MODEL slx_1dac27b51b91
CONFIG AbsTol = auto
CONFIG EnableMultiTasking = on
CONFIG FixedStep = 0.001
CONFIG MaxStep = auto
CONFIG MinStep = auto
CONFIG RelTol = 1e-3
CONFIG SampleTimeConstraint = Unconstrained
CONFIG Solver = ode14x
CONFIG SolverName = ode14x
CONFIG StartTime = 0.0
CONFIG StopTime = 15
BLOCK [SubSystem] Cascade
  Ports = []
  RequestExecContextInheritance = off
BLOCK [From] Cascade/Actual ouput
  GotoTag = Y
BLOCK [Sum] Cascade/Add1
  IconShape = rectangular
  Ports = [2, 1]
BLOCK [From] Cascade/Disturbance Input
  GotoTag = D
BLOCK [From] Cascade/Error
  GotoTag = E
BLOCK [Gain] Cascade/Force to Voltage
  Gain = 1/ 2871.14
BLOCK [FromWorkspace] Cascade/From Workspace2
  OutDataTypeStr = double
  OutputAfterFinalValue = Setting to zero
  VariableName = Cut1500down
BLOCK [Gain] Cascade/Gain3
  Gain = gain_P
BLOCK [Gain] Cascade/Gain4
  Gain = gain_V_I
BLOCK [Gain] Cascade/Gain5
  Gain = gain_V_P
BLOCK [Goto] Cascade/Goto
  GotoTag = D
BLOCK [Goto] Cascade/Goto1
  GotoTag = R
BLOCK [Goto] Cascade/Goto2
  GotoTag = E
BLOCK [Goto] Cascade/Goto3
  GotoTag = Y
BLOCK [Integrator] Cascade/Integrator1
  InitialCondition = .1
  Ports = [1, 1]
BLOCK [ManualSwitch] Cascade/Manual Switch
  NameLocation = left
BLOCK [Scope] Cascade/Output Position (mm)
  Floating = off
  NumInputPorts = 1
  Ports = [1]
  ScopeSpecificationString = Simulink.scopes.TimeScopeBlockCfg('CurrentConfiguration', extmgr.ConfigurationSet(extmgr.Configuration('Core','General UI',true),extmgr.Configuration('Core','Source UI',true),extmgr.Configuration('Sources','WiredSimulink',true,'DataLoggingVariableName','ScopeData2'),extmgr.Configuration('Visuals','Time Domain',true,'SerializedDisplays',{struct('MinYLimReal','-66692021064882830098913468871871206665...<+3796ch>
BLOCK [TransferFcn] Cascade/Plant (Googol Tech)
  Denominator = [1 163 193.3]
  Numerator = [78020]
BLOCK [Sin] Cascade/Ref. Position, Xref (mm)
  Amplitude = 5
  Frequency = 0.5*(2*pi)
  Offset = 1/2000
  Ports = [0, 1]
  SampleTime = 0
BLOCK [From] Cascade/Reference Input
  GotoTag = R
BLOCK [Saturate] Cascade/Saturation
  LowerLimit = -92
  UpperLimit = 92
BLOCK [Scope] Cascade/Scope
  Floating = off
  NumInputPorts = 4
  Ports = [4]
  ScopeSpecificationString = Simulink.scopes.TimeScopeBlockCfg('CurrentConfiguration', extmgr.ConfigurationSet(extmgr.Configuration('Core','General UI',true),extmgr.Configuration('Core','Source UI',true),extmgr.Configuration('Sources','WiredSimulink',true,'DataLoggingVariableName','cascade','DataLogging',true,'DataLoggingSaveFormat','StructureWithTime'),extmgr.Configuration('Visuals','Time Domain',true,'SerializedDisplays',{s...<+3904ch>
BLOCK [Sum] Cascade/Sum1
  Inputs = ++|
  Ports = [2, 1]
BLOCK [Sum] Cascade/Sum3
  Inputs = |+-
  NameLocation = top
  Ports = [2, 1]
BLOCK [Sum] Cascade/Sum4
  Inputs = |+-
  NameLocation = top
  Ports = [2, 1]
BLOCK [TransportDelay] Cascade/TIme Delay
  DelayTime = 0.0012
  Ports = [1, 1]
BLOCK [TransferFcn] Cascade/V est
  Denominator = [1 942.5]
  Numerator = [942.5, 0]
BLOCK [SubSystem] Model Based Design
  Commented = on
  Ports = [0, 0, 0, 0, 0, 1]
  RequestExecContextInheritance = off
BLOCK [Scope] Model Based Design/Axis Cmd
  Floating = off
  NumInputPorts = 2
  Ports = [2]
  ScopeSpecificationString = Simulink.scopes.TimeScopeBlockCfg('CurrentConfiguration', extmgr.ConfigurationSet(extmgr.Configuration('Core','General UI',true),extmgr.Configuration('Core','Source UI',true),extmgr.Configuration('Sources','WiredSimulink',true),extmgr.Configuration('Visuals','Time Domain',true,'SerializedDisplays',{struct('MinYLimReal','-0.06054','MaxYLimReal','0.06145','YLabelReal','','MinYLimMag','0.00000','MaxY...<+1365ch>
BLOCK [Reference] Model Based Design/Base  REF=sm_lib/Body Elements/Brick Solid
  Ports = [0, 0, 0, 0, 0, 1, 1]
  SourceBlock = sm_lib/Body Elements/Brick Solid
  SourceProductBaseCode = MS
  SourceType = Brick Solid
BLOCK [From] Model Based Design/From
  GotoTag = Ycmd
  TagVisibility = global
BLOCK [From] Model Based Design/From1
  GotoTag = Xcmd
  TagVisibility = global
BLOCK [From] Model Based Design/From2
  GotoTag = Ycmd
  TagVisibility = global
BLOCK [From] Model Based Design/From3
  GotoTag = Xcmd
  TagVisibility = global
BLOCK [From] Model Based Design/From4
  GotoTag = Px
  TagVisibility = global
BLOCK [From] Model Based Design/From5
  GotoTag = Vx
  TagVisibility = global
BLOCK [From] Model Based Design/From6
  GotoTag = Py
  TagVisibility = global
BLOCK [From] Model Based Design/From7
  GotoTag = Vy
  TagVisibility = global
BLOCK [From] Model Based Design/From8
  GotoTag = Px
  TagVisibility = global
BLOCK [From] Model Based Design/From9
  GotoTag = Py
  TagVisibility = global
BLOCK [Goto] Model Based Design/Goto
  GotoTag = Px
  TagVisibility = global
BLOCK [Goto] Model Based Design/Goto1
  GotoTag = Vx
  TagVisibility = global
BLOCK [Goto] Model Based Design/Goto2
  GotoTag = Py
  TagVisibility = global
BLOCK [Goto] Model Based Design/Goto3
  GotoTag = Vy
  TagVisibility = global
BLOCK [Reference] Model Based Design/PS-Simulink Converter  REF=nesl_utility/PS-Simulink
Converter
  Ports = [0, 1, 0, 0, 0, 1]
  SourceBlock = nesl_utility/PS-Simulink
Converter
  SourceProductBaseCode = SS
  SourceType = PS-Simulink
Converter
BLOCK [Reference] Model Based Design/PS-Simulink Converter1  REF=nesl_utility/PS-Simulink
Converter
  Ports = [0, 1, 0, 0, 0, 1]
  SourceBlock = nesl_utility/PS-Simulink
Converter
  SourceProductBaseCode = SS
  SourceType = PS-Simulink
Converter
BLOCK [Reference] Model Based Design/PS-Simulink Converter2  REF=nesl_utility/PS-Simulink
Converter
  Ports = [0, 1, 0, 0, 0, 1]
  SourceBlock = nesl_utility/PS-Simulink
Converter
  SourceProductBaseCode = SS
  SourceType = PS-Simulink
Converter
BLOCK [Reference] Model Based Design/PS-Simulink Converter3  REF=nesl_utility/PS-Simulink
Converter
  Ports = [0, 1, 0, 0, 0, 1]
  SourceBlock = nesl_utility/PS-Simulink
Converter
  SourceProductBaseCode = SS
  SourceType = PS-Simulink
Converter
BLOCK [Scope] Model Based Design/Position, Velocity
  Floating = off
  NumInputPorts = 4
  Ports = [4]
  ScopeSpecificationString = Simulink.scopes.TimeScopeBlockCfg('CurrentConfiguration', extmgr.ConfigurationSet(extmgr.Configuration('Core','General UI',true),extmgr.Configuration('Core','Source UI',true),extmgr.Configuration('Sources','WiredSimulink',true,'DataLoggingVariableName','ScopeData1'),extmgr.Configuration('Visuals','Time Domain',true,'SerializedDisplays',{struct('MinYLimReal','-0.0575','MaxYLimReal','0.0575','YLabel...<+3923ch>
BLOCK [Reference] Model Based Design/Prismatic X-axis  REF=sm_lib/Joints/Prismatic
Joint
  Ports = [0, 0, 0, 0, 0, 2, 3]
  SourceBlock = sm_lib/Joints/Prismatic
Joint
  SourceProductBaseCode = MS
  SourceType = Prismatic
Joint
BLOCK [Reference] Model Based Design/Prismatic Y-axis  REF=sm_lib/Joints/Prismatic
Joint
  Ports = [0, 0, 0, 0, 0, 2, 3]
  SourceBlock = sm_lib/Joints/Prismatic
Joint
  SourceProductBaseCode = MS
  SourceType = Prismatic
Joint
BLOCK [Reference] Model Based Design/Rigid Transform1  REF=sm_lib/Frames and
Transforms/Rigid
Transform
  Ports = [0, 0, 0, 0, 0, 1, 1]
  SourceBlock = sm_lib/Frames and
Transforms/Rigid
Transform
  SourceProductBaseCode = MS
  SourceType = Rigid
Transform
BLOCK [SubSystem] Model Based Design/S2m
  Ports = [1, 0, 0, 0, 0, 0, 1]
  RequestExecContextInheritance = off
  ShowPortLabels = none
BLOCK [Inport] Model Based Design/S2m/In
BLOCK [PMIOPort] Model Based Design/S2m/Out
  Side = Right
BLOCK [Reference] Model Based Design/S2m/mm  REF=nesl_utility/Simulink-PS
Converter
  Ports = [1, 0, 0, 0, 0, 0, 1]
  SourceBlock = nesl_utility/Simulink-PS
Converter
  SourceProductBaseCode = MT,SS
  SourceType = Simulink-PS
Converter
BLOCK [SubSystem] Model Based Design/S2m1
  Ports = [1, 0, 0, 0, 0, 0, 1]
  RequestExecContextInheritance = off
  ShowPortLabels = none
BLOCK [Inport] Model Based Design/S2m1/In
BLOCK [PMIOPort] Model Based Design/S2m1/Prismatic Y-axis
  Side = Right
BLOCK [Reference] Model Based Design/S2m1/mm  REF=nesl_utility/Simulink-PS
Converter
  Ports = [1, 0, 0, 0, 0, 0, 1]
  SourceBlock = nesl_utility/Simulink-PS
Converter
  SourceProductBaseCode = MT,SS
  SourceType = Simulink-PS
Converter
BLOCK [SubSystem] Model Based Design/Subsystem
  Ports = []
  RequestExecContextInheritance = off
BLOCK [Reference] Model Based Design/Subsystem/Band-Limited White Noise  REF=simulink/Sources/Band-Limited
White Noise
  NameLocation = right
  Ports = [0, 1]
  SourceBlock = simulink/Sources/Band-Limited
White Noise
  SourceProductBaseCode = SL
  SourceType = Band-Limited White Noise.
BLOCK [Goto] Model Based Design/Subsystem/Goto
  GotoTag = Ycmd
  TagVisibility = global
BLOCK [Goto] Model Based Design/Subsystem/Goto1
  GotoTag = Xcmd
  TagVisibility = global
BLOCK [Saturate] Model Based Design/Subsystem/Saturation
  LowerLimit = -.2
  UpperLimit = .2
BLOCK [Saturate] Model Based Design/Subsystem/Saturation1
  LowerLimit = -.1
  UpperLimit = .1
BLOCK [Sin] Model Based Design/Subsystem/Sine Wave X
  Amplitude = ax
  Frequency = Fx
  Ports = [0, 1]
  SampleTime = 0
BLOCK [Sin] Model Based Design/Subsystem/Sine Wave Y
  Amplitude = ay
  Frequency = Fy
  Phase = 8
  Ports = [0, 1]
  SampleTime = 0
BLOCK [Sum] Model Based Design/Subsystem/Sum
  Inputs = |++
  Ports = [2, 1]
BLOCK [TransferFcn] Model Based Design/Subsystem/Transfer Fcn
  Denominator = [1 163 193.3]
  Numerator = [72080]
BLOCK [TransportDelay] Model Based Design/Subsystem/Transport Delay2
  DelayTime = 0.0012
  Ports = [1, 1]
BLOCK [SubSystem] Model Based Design/World Config
  NameLocation = top
  Ports = [0, 0, 0, 0, 0, 0, 1]
  RequestExecContextInheritance = off
BLOCK [Reference] Model Based Design/World Config/Mechanism Configuration  REF=sm_lib/Utilities/Mechanism
Configuration
  Ports = [0, 0, 0, 0, 0, 0, 1]
  SourceBlock = sm_lib/Utilities/Mechanism
Configuration
  SourceProductBaseCode = MS
  SourceType = Mechanism
Configuration
BLOCK [PMIOPort] Model Based Design/World Config/Mechanism Configuration1
  Side = Right
BLOCK [Reference] Model Based Design/World Config/Solver Configuration  REF=nesl_utility/Solver
Configuration
  Ports = [0, 0, 0, 0, 0, 0, 1]
  SourceBlock = nesl_utility/Solver
Configuration
  SourceProductBaseCode = MT,SS
  SourceType = Solver
Configuration
BLOCK [Reference] Model Based Design/World Config/World Frame  REF=sm_lib/Frames and
Transforms/World Frame
  Ports = [0, 0, 0, 0, 0, 0, 1]
  SourceBlock = sm_lib/Frames and
Transforms/World Frame
  SourceProductBaseCode = MS
  SourceType = World Frame
BLOCK [Reference] Model Based Design/X-axis  REF=sm_lib/Body Elements/Brick Solid
  Ports = [0, 0, 0, 0, 0, 1, 1]
  SourceBlock = sm_lib/Body Elements/Brick Solid
  SourceProductBaseCode = MS
  SourceType = Brick Solid
BLOCK [Reference] Model Based Design/XY Position  REF=simulink/Sinks/XY Graph
  Ports = [2]
  SourceBlock = simulink/Sinks/XY Graph
  SourceProductBaseCode = SL
  SourceType = XY scope.
BLOCK [Reference] Model Based Design/Y-axis  REF=sm_lib/Body Elements/Brick Solid
  Ports = [0, 0, 0, 0, 0, 1, 1]
  SourceBlock = sm_lib/Body Elements/Brick Solid
  SourceProductBaseCode = MS
  SourceType = Brick Solid
BLOCK [Reference] Model Based Design/Y-axis Transform  REF=sm_lib/Frames and
Transforms/Rigid
Transform
  Ports = [0, 0, 0, 0, 0, 1, 1]
  SourceBlock = sm_lib/Frames and
Transforms/Rigid
Transform
  SourceProductBaseCode = MS
  SourceType = Rigid
Transform
BLOCK [Reference] Model Based Design/Y-top  REF=sm_lib/Body Elements/Brick Solid
  Ports = [0, 0, 0, 0, 0, 1, 1]
  SourceBlock = sm_lib/Body Elements/Brick Solid
  SourceProductBaseCode = MS
  SourceType = Brick Solid
BLOCK [PMIOPort] Model Based Design/Y-top1
  Side = Left
BLOCK [SubSystem] PID
  Commented = on
  Ports = []
  RequestExecContextInheritance = off
BLOCK [From] PID/Actual ouput
  GotoTag = Y
BLOCK [Scope] PID/Actual position
  Floating = off
  NumInputPorts = 1
  Ports = [1]
  ScopeSpecificationString = Simulink.scopes.TimeScopeBlockCfg('CurrentConfiguration', extmgr.ConfigurationSet(extmgr.Configuration('Core','General UI',true),extmgr.Configuration('Core','Source UI',true),extmgr.Configuration('Sources','WiredSimulink',true,'DataLoggingVariableName','PID_ActualPosition','DataLoggingSaveFormat','Array'),extmgr.Configuration('Visuals','Time Domain',true,'SerializedDisplays',{struct('MinYLimReal',...<+1431ch>
BLOCK [Sum] PID/Add
  IconShape = rectangular
  Inputs = +++
  Ports = [3, 1]
BLOCK [Derivative] PID/Derivative
BLOCK [From] PID/Disturbance Input
  GotoTag = D
BLOCK [From] PID/Error
  GotoTag = E
BLOCK [Gain] PID/Force to Voltage
  Gain = 1/ 2871.14
BLOCK [FromWorkspace] PID/From Workspace2
  OutDataTypeStr = double
  OutputAfterFinalValue = Setting to zero
  VariableName = Cut1500down
BLOCK [Gain] PID/Gain
  Gain = new_kd
BLOCK [Gain] PID/Gain1
  Gain = new_ki
BLOCK [Gain] PID/Gain2
  Gain = new_kp
  NameLocation = right
BLOCK [Goto] PID/Goto
  GotoTag = D
BLOCK [Goto] PID/Goto1
  GotoTag = R
BLOCK [Goto] PID/Goto2
  GotoTag = E
BLOCK [Goto] PID/Goto3
  GotoTag = Y
BLOCK [Integrator] PID/Integrator
  Ports = [1, 1]
BLOCK [ManualSwitch] PID/Manual Switch1
  CurrentSetting = 0
  NameLocation = left
BLOCK [TransferFcn] PID/Plant (Googol Tech)
  Denominator = [1 163 193.3]
  Numerator = [78020]
BLOCK [Sin] PID/Ref. Position, Xref (mm)
  Amplitude = 5
  Frequency = 0.5*(2*pi)
  Offset = 1/2000
  Ports = [0, 1]
  SampleTime = 0
BLOCK [From] PID/Reference Input
  GotoTag = R
BLOCK [Saturate] PID/Saturation1
  LowerLimit = -92
  UpperLimit = 92
BLOCK [Scope] PID/Scope
  Floating = off
  NumInputPorts = 4
  Ports = [4]
  ScopeSpecificationString = Simulink.scopes.TimeScopeBlockCfg('CurrentConfiguration', extmgr.ConfigurationSet(extmgr.Configuration('Core','General UI',true),extmgr.Configuration('Core','Source UI',true),extmgr.Configuration('Sources','WiredSimulink',true,'DataLoggingVariableName','PID','DataLogging',true,'DataLoggingSaveFormat','StructureWithTime'),extmgr.Configuration('Visuals','Time Domain',true,'SerializedDisplays',{struc...<+3842ch>
BLOCK [Sum] PID/Sum
  Inputs = ++|
  Ports = [2, 1]
BLOCK [Sum] PID/Sum2
  Inputs = |+-
  NameLocation = top
  Ports = [2, 1]
BLOCK [TransportDelay] PID/TIme Delay
  DelayTime = 0.0012
  Ports = [1, 1]
BLOCK [SubSystem] SMC
  Commented = on
  Ports = []
  RequestExecContextInheritance = off
BLOCK [From] SMC/Actual ouput
  GotoTag = Y
BLOCK [Scope] SMC/Actual position
  Floating = off
  NumInputPorts = 1
  Ports = [1]
  ScopeSpecificationString = Simulink.scopes.TimeScopeBlockCfg('CurrentConfiguration', extmgr.ConfigurationSet(extmgr.Configuration('Core','General UI',true),extmgr.Configuration('Core','Source UI',true),extmgr.Configuration('Sources','WiredSimulink',true,'DataLoggingVariableName','ScopeData1'),extmgr.Configuration('Visuals','Time Domain',true,'SerializedDisplays',{struct('MinYLimReal','-235.24396','MaxYLimReal','662.41077','...<+1446ch>
BLOCK [Scope] SMC/Actual position1
  Commented = on
  Floating = off
  NumInputPorts = 1
  Ports = [1]
  ScopeSpecificationString = Simulink.scopes.TimeScopeBlockCfg('CurrentConfiguration', extmgr.ConfigurationSet(extmgr.Configuration('Core','General UI',true),extmgr.Configuration('Core','Source UI',true),extmgr.Configuration('Sources','WiredSimulink',true,'DataLoggingVariableName','ScopeData1'),extmgr.Configuration('Visuals','Time Domain',true,'SerializedDisplays',{struct('MinYLimReal','-32969.8446','MaxYLimReal','32938.39501...<+1458ch>
BLOCK [Sum] SMC/Add
  IconShape = rectangular
  Inputs = -+
  Ports = [2, 1]
BLOCK [Sum] SMC/Add1
  IconShape = rectangular
  Inputs = +-
  NameLocation = top
  Ports = [2, 1]
BLOCK [Sum] SMC/Add10
  Commented = on
  IconShape = rectangular
  Inputs = +-
  Ports = [2, 1]
BLOCK [Sum] SMC/Add2
  IconShape = rectangular
  Ports = [2, 1]
BLOCK [Sum] SMC/Add3
  IconShape = rectangular
  Inputs = -+
  Ports = [2, 1]
BLOCK [Sum] SMC/Add4
  IconShape = rectangular
  Inputs = +++-
  NameLocation = top
  Ports = [4, 1]
BLOCK [Sum] SMC/Add5
  Commented = on
  IconShape = rectangular
  Inputs = +-
  Ports = [2, 1]
BLOCK [Sum] SMC/Add6
  Commented = on
  IconShape = rectangular
  Inputs = +-
  Ports = [2, 1]
BLOCK [Sum] SMC/Add8
  Commented = on
  IconShape = rectangular
  Inputs = -+
  Ports = [2, 1]
BLOCK [Sum] SMC/Add9
  Commented = on
  IconShape = rectangular
  Inputs = ++++++
  NameLocation = top
  Ports = [6, 1]
BLOCK [Derivative] SMC/Derivative1
  NameLocation = left
BLOCK [From] SMC/Disturbance Input
  GotoTag = D
BLOCK [From] SMC/Error
  GotoTag = E
BLOCK [Gain] SMC/Force to Voltage1
  Gain = 1/ 2871.14
BLOCK [Gain] SMC/Force to Voltage2
  Commented = on
  Gain = 1/ 2871.14
BLOCK [FromWorkspace] SMC/From Workspace1
  Commented = on
  OutDataTypeStr = double
  OutputAfterFinalValue = Setting to zero
  VariableName = Cut1500down
BLOCK [FromWorkspace] SMC/From Workspace2
  OutDataTypeStr = double
  OutputAfterFinalValue = Setting to zero
  VariableName = Cut1500down
BLOCK [Gain] SMC/Gain
  Gain = 163
  NameLocation = top
BLOCK [Gain] SMC/Gain (K)
  Gain = 0.4
BLOCK [Gain] SMC/Gain (K)1
  Commented = on
  Gain = 20
BLOCK [Gain] SMC/Gain1
  Gain = 193.3
  NameLocation = top
BLOCK [Gain] SMC/Gain2
  Commented = on
  Gain = 0.0012
  NameLocation = top
BLOCK [Gain] SMC/Gain3
  Commented = on
  Gain = 0.0024*lamda
  NameLocation = top
BLOCK [Gain] SMC/Gain4
  Gain = 1/78020
  NameLocation = top
BLOCK [Gain] SMC/Gain5
  Commented = on
  Gain = 1/78020
  NameLocation = top
BLOCK [Gain] SMC/Gain6
  Commented = on
  Gain = 0.0012*lamda*lamda
  NameLocation = top
BLOCK [Gain] SMC/Gain7
  Commented = on
  Gain = 0.0012
  NameLocation = top
BLOCK [Goto] SMC/Goto1
  GotoTag = R
BLOCK [Goto] SMC/Goto2
  GotoTag = E
BLOCK [Goto] SMC/Goto3
  GotoTag = Y
BLOCK [Goto] SMC/Goto4
  GotoTag = D
BLOCK [Goto] SMC/Goto5
  Commented = on
  GotoTag = R
BLOCK [Goto] SMC/Goto6
  Commented = on
  GotoTag = E
BLOCK [Goto] SMC/Goto7
  Commented = on
  GotoTag = Y
BLOCK [Goto] SMC/Goto8
  Commented = on
  GotoTag = D
BLOCK [Gain] SMC/Lamda
  Gain = lamda
BLOCK [Gain] SMC/Lamda1
  Gain = lamda
BLOCK [Gain] SMC/Lamda2
  Commented = on
  Gain = lamda*lamda
BLOCK [Gain] SMC/Lamda3
  Commented = on
  Gain = 1.1956
BLOCK [Gain] SMC/Lamda4
  Commented = on
  Gain = lamda*2
BLOCK [Gain] SMC/Lamda5
  Commented = on
  Gain = 163.2319
BLOCK [TransferFcn] SMC/Plant (Googol Tech)
  Denominator = [1 163 193.3]
  Numerator = [78020]
BLOCK [TransferFcn] SMC/Plant (Googol Tech)1
  Commented = on
  Denominator = [1 163 193.3]
  Numerator = [78020]
BLOCK [Sin] SMC/Ref. Position, Xref (mm)
  Amplitude = 5
  Frequency = 0.5*(2*pi)
  Offset = 1/2000
  Ports = [0, 1]
  SampleTime = 0
BLOCK [Sin] SMC/Ref. Position, Xref (mm)1
  Amplitude = 5
  Commented = on
  Frequency = 0.5*(2*pi)
  Offset = 1/2000
  Ports = [0, 1]
  SampleTime = 0
BLOCK [From] SMC/Reference Input
  GotoTag = R
BLOCK [Saturate] SMC/Saturation
  LowerLimit = -92
  UpperLimit = 92
BLOCK [Saturate] SMC/Saturation1
  Commented = on
  LowerLimit = -92
  UpperLimit = 92
BLOCK [Scope] SMC/Scope
  Floating = off
  NumInputPorts = 4
  Ports = [4]
  ScopeSpecificationString = Simulink.scopes.TimeScopeBlockCfg('CurrentConfiguration', extmgr.ConfigurationSet(extmgr.Configuration('Core','General UI',true),extmgr.Configuration('Core','Source UI',true),extmgr.Configuration('Sources','WiredSimulink',true,'DataLoggingVariableName','ScopeData2'),extmgr.Configuration('Visuals','Time Domain',true,'SerializedDisplays',{struct('MinYLimReal','-0.01872','MaxYLimReal','0.01075','YLab...<+3419ch>
BLOCK [Signum] SMC/Sign
BLOCK [Signum] SMC/Sign1
  Commented = on
BLOCK [SubSystem] SMC/Subsystem
  Ports = [1, 2]
  RequestExecContextInheritance = off
BLOCK [Derivative] SMC/Subsystem/Derivative2
BLOCK [Derivative] SMC/Subsystem/Derivative3
BLOCK [Outport] SMC/Subsystem/y_ddot
BLOCK [Outport] SMC/Subsystem/y_dot
  Port = 2
BLOCK [Inport] SMC/Subsystem/yd
BLOCK [SubSystem] SMC/Subsystem1
  Commented = on
  Ports = [1, 3]
  RequestExecContextInheritance = off
BLOCK [Derivative] SMC/Subsystem1/Derivative1
BLOCK [Derivative] SMC/Subsystem1/Derivative2
BLOCK [Derivative] SMC/Subsystem1/Derivative3
BLOCK [Inport] SMC/Subsystem1/yd
BLOCK [Outport] SMC/Subsystem1/yd_3dot
  Port = 3
BLOCK [Outport] SMC/Subsystem1/yd_ddot
  Port = 2
BLOCK [Outport] SMC/Subsystem1/yd_dot
BLOCK [SubSystem] SMC/Subsystem2
  Commented = on
  Ports = [1, 3]
  RequestExecContextInheritance = off
BLOCK [Derivative] SMC/Subsystem2/Derivative1
BLOCK [Derivative] SMC/Subsystem2/Derivative2
BLOCK [Derivative] SMC/Subsystem2/Derivative3
BLOCK [Inport] SMC/Subsystem2/y
BLOCK [Outport] SMC/Subsystem2/y_3dot
  Port = 3
BLOCK [Outport] SMC/Subsystem2/y_ddot
  Port = 2
BLOCK [Outport] SMC/Subsystem2/y_dot
BLOCK [Sum] SMC/Sum
  Inputs = ++|
  Ports = [2, 1]
BLOCK [Sum] SMC/Sum1
  Commented = on
  Inputs = ++|
  Ports = [2, 1]
BLOCK [Sum] SMC/Sum2
  Commented = on
  Inputs = +++
  Ports = [3, 1]
BLOCK [TransportDelay] SMC/TIme Delay1
  Commented = on
  DelayTime = 0.0012
  Ports = [1, 1]
BLOCK [Terminator] SMC/Terminator
  Commented = on
  NameLocation = left
LINE Cascade/Actual ouput:1 -> Cascade/Scope:4
LINE Cascade/Add1:1 -> Cascade/Sum1:2
LINE Cascade/Disturbance Input:1 -> Cascade/Scope:1
LINE Cascade/Error:1 -> Cascade/Scope:2
LINE Cascade/Force to Voltage:1 -> Cascade/Goto:1
LINE Cascade/Force to Voltage:1 -> Cascade/Manual Switch:1
LINE Cascade/From Workspace2:1 -> Cascade/Force to Voltage:1
LINE Cascade/Gain3:1 -> Cascade/Sum3:1
LINE Cascade/Gain4:1 -> Cascade/Integrator1:1
LINE Cascade/Gain5:1 -> Cascade/Add1:1
LINE Cascade/Integrator1:1 -> Cascade/Add1:2
LINE Cascade/Manual Switch:1 -> Cascade/Sum1:1
LINE Cascade/Plant (Googol Tech):1 -> Cascade/TIme Delay:1
LINE Cascade/Ref. Position, Xref (mm):1 -> Cascade/Goto1:1
LINE Cascade/Ref. Position, Xref (mm):1 -> Cascade/Sum4:1
LINE Cascade/Reference Input:1 -> Cascade/Scope:3
LINE Cascade/Saturation:1 -> Cascade/Plant (Googol Tech):1
LINE Cascade/Sum1:1 -> Cascade/Saturation:1
LINE Cascade/Sum3:1 -> Cascade/Gain4:1
LINE Cascade/Sum3:1 -> Cascade/Gain5:1
LINE Cascade/Sum4:1 -> Cascade/Gain3:1
LINE Cascade/Sum4:1 -> Cascade/Goto2:1
LINE Cascade/TIme Delay:1 -> Cascade/Goto3:1
LINE Cascade/TIme Delay:1 -> Cascade/Output Position (mm):1
LINE Cascade/TIme Delay:1 -> Cascade/Sum4:2
LINE Cascade/TIme Delay:1 -> Cascade/V est:1
LINE Cascade/V est:1 -> Cascade/Sum3:2
LINE Model Based Design/Base:rconn -> Model Based Design/World Config:rconn
LINE Model Based Design/From1:1 -> Model Based Design/S2m:1
LINE Model Based Design/From2:1 -> Model Based Design/Axis Cmd:2
LINE Model Based Design/From3:1 -> Model Based Design/Axis Cmd:1
LINE Model Based Design/From4:1 -> Model Based Design/XY Position:2
LINE Model Based Design/From5:1 -> Model Based Design/Position, Velocity:3
LINE Model Based Design/From6:1 -> Model Based Design/XY Position:1
LINE Model Based Design/From7:1 -> Model Based Design/Position, Velocity:4
LINE Model Based Design/From8:1 -> Model Based Design/Position, Velocity:2
LINE Model Based Design/From9:1 -> Model Based Design/Position, Velocity:1
LINE Model Based Design/From:1 -> Model Based Design/S2m1:1
LINE Model Based Design/PS-Simulink Converter1:1 -> Model Based Design/Goto1:1
LINE Model Based Design/PS-Simulink Converter1:lconn -> Model Based Design/Prismatic X-axis:rconn
LINE Model Based Design/PS-Simulink Converter2:1 -> Model Based Design/Goto2:1
LINE Model Based Design/PS-Simulink Converter2:lconn -> Model Based Design/Prismatic Y-axis:rconn
LINE Model Based Design/PS-Simulink Converter3:1 -> Model Based Design/Goto3:1
LINE Model Based Design/PS-Simulink Converter3:lconn -> Model Based Design/Prismatic Y-axis:rconn
LINE Model Based Design/PS-Simulink Converter:1 -> Model Based Design/Goto:1
LINE Model Based Design/PS-Simulink Converter:lconn -> Model Based Design/Prismatic X-axis:rconn
LINE Model Based Design/Prismatic Y-axis:lconn -> Model Based Design/Y-axis:lconn
LINE Model Based Design/Prismatic Y-axis:rconn -> Model Based Design/Rigid Transform1:lconn
LINE Model Based Design/Rigid Transform1:rconn -> Model Based Design/Y-top:rconn
LINE Model Based Design/S2m/In:1 -> Model Based Design/S2m/mm:1
LINE Model Based Design/S2m/mm:rconn -> Model Based Design/S2m/Out:rconn
LINE Model Based Design/S2m1/In:1 -> Model Based Design/S2m1/mm:1
LINE Model Based Design/S2m1/mm:rconn -> Model Based Design/S2m1/Prismatic Y-axis:rconn
LINE Model Based Design/S2m1:rconn -> Model Based Design/Prismatic Y-axis:lconn
LINE Model Based Design/S2m:rconn -> Model Based Design/Prismatic X-axis:lconn
LINE Model Based Design/Subsystem/Band-Limited White Noise:1 -> Model Based Design/Subsystem/Sum:2
LINE Model Based Design/Subsystem/Saturation1:1 -> Model Based Design/Subsystem/Goto:1
LINE Model Based Design/Subsystem/Saturation:1 -> Model Based Design/Subsystem/Sum:1
LINE Model Based Design/Subsystem/Sine Wave X:1 -> Model Based Design/Subsystem/Saturation:1
LINE Model Based Design/Subsystem/Sine Wave Y:1 -> Model Based Design/Subsystem/Saturation1:1
LINE Model Based Design/Subsystem/Sum:1 -> Model Based Design/Subsystem/Transfer Fcn:1
LINE Model Based Design/Subsystem/Transfer Fcn:1 -> Model Based Design/Subsystem/Transport Delay2:1
LINE Model Based Design/Subsystem/Transport Delay2:1 -> Model Based Design/Subsystem/Goto1:1
LINE Model Based Design/World Config/World Frame:rconn -> Model Based Design/World Config/Solver Configuration:rconn
LINE Model Based Design/X-axis:lconn -> Model Based Design/Prismatic X-axis:lconn
LINE Model Based Design/X-axis:rconn -> Model Based Design/Base:lconn
LINE Model Based Design/Y-axis Transform:lconn -> Model Based Design/Prismatic X-axis:rconn
LINE Model Based Design/Y-axis:rconn -> Model Based Design/Y-axis Transform:rconn
LINE Model Based Design/Y-top:lconn -> Model Based Design/Y-top1:rconn
LINE PID/Actual ouput:1 -> PID/Scope:4
LINE PID/Add:1 -> PID/Sum:2
LINE PID/Derivative:1 -> PID/Add:3
LINE PID/Disturbance Input:1 -> PID/Scope:1
LINE PID/Error:1 -> PID/Scope:2
LINE PID/Force to Voltage:1 -> PID/Goto:1
LINE PID/Force to Voltage:1 -> PID/Manual Switch1:1
LINE PID/From Workspace2:1 -> PID/Force to Voltage:1
LINE PID/Gain1:1 -> PID/Integrator:1
LINE PID/Gain2:1 -> PID/Add:1
LINE PID/Gain:1 -> PID/Derivative:1
LINE PID/Integrator:1 -> PID/Add:2
LINE PID/Manual Switch1:1 -> PID/Sum:1
LINE PID/Plant (Googol Tech):1 -> PID/TIme Delay:1
LINE PID/Ref. Position, Xref (mm):1 -> PID/Goto1:1
LINE PID/Ref. Position, Xref (mm):1 -> PID/Sum2:1
LINE PID/Reference Input:1 -> PID/Scope:3
LINE PID/Saturation1:1 -> PID/Plant (Googol Tech):1
LINE PID/Sum2:1 -> PID/Gain1:1
LINE PID/Sum2:1 -> PID/Gain2:1
LINE PID/Sum2:1 -> PID/Gain:1
LINE PID/Sum2:1 -> PID/Goto2:1
LINE PID/Sum:1 -> PID/Saturation1:1
LINE PID/TIme Delay:1 -> PID/Actual position:1
LINE PID/TIme Delay:1 -> PID/Goto3:1
LINE PID/TIme Delay:1 -> PID/Sum2:2
LINE SMC/Actual ouput:1 -> SMC/Scope:4
LINE SMC/Add10:1 -> SMC/Gain3:1
LINE SMC/Add10:1 -> SMC/Sum2:3
LINE SMC/Add1:1 -> SMC/Add2:2
LINE SMC/Add1:1 -> SMC/Lamda1:1
LINE SMC/Add2:1 -> SMC/Sign:1
LINE SMC/Add3:1 -> SMC/Sum:2
LINE SMC/Add4:1 -> SMC/Gain4:1
LINE SMC/Add5:1 -> SMC/Goto6:1
LINE SMC/Add5:1 -> SMC/Lamda2:1
LINE SMC/Add6:1 -> SMC/Lamda4:1
LINE SMC/Add8:1 -> SMC/Sum1:2
LINE SMC/Add9:1 -> SMC/Gain5:1
LINE SMC/Add:1 -> SMC/Goto2:1
LINE SMC/Add:1 -> SMC/Lamda:1
LINE SMC/Derivative1:1 -> SMC/Add1:1
LINE SMC/Derivative1:1 -> SMC/Gain:1
LINE SMC/Disturbance Input:1 -> SMC/Scope:1
LINE SMC/Error:1 -> SMC/Scope:2
LINE SMC/Force to Voltage1:1 -> SMC/Goto4:1
LINE SMC/Force to Voltage1:1 -> SMC/Sum:1
LINE SMC/Force to Voltage2:1 -> SMC/Goto8:1
LINE SMC/Force to Voltage2:1 -> SMC/Sum1:1
LINE SMC/From Workspace1:1 -> SMC/Force to Voltage2:1
LINE SMC/From Workspace2:1 -> SMC/Force to Voltage1:1
LINE SMC/Gain (K)1:1 -> SMC/Add8:1
LINE SMC/Gain (K):1 -> SMC/Add3:1
LINE SMC/Gain1:1 -> SMC/Add4:2
LINE SMC/Gain2:1 -> SMC/Add9:1
LINE SMC/Gain3:1 -> SMC/Add9:2
LINE SMC/Gain4:1 -> SMC/Add3:2
LINE SMC/Gain5:1 -> SMC/Add8:2
LINE SMC/Gain6:1 -> SMC/Add9:3
LINE SMC/Gain7:1 -> SMC/Add9:6
LINE SMC/Gain:1 -> SMC/Add4:1
LINE SMC/Lamda1:1 -> SMC/Add4:4
LINE SMC/Lamda2:1 -> SMC/Gain6:1
LINE SMC/Lamda2:1 -> SMC/Sum2:1
LINE SMC/Lamda3:1 -> SMC/Add9:4
LINE SMC/Lamda4:1 -> SMC/Sum2:2
LINE SMC/Lamda5:1 -> SMC/Add9:5
LINE SMC/Lamda:1 -> SMC/Add2:1
LINE SMC/Plant (Googol Tech)1:1 -> SMC/TIme Delay1:1
LINE SMC/Plant (Googol Tech):1 -> SMC/Actual position:1
LINE SMC/Plant (Googol Tech):1 -> SMC/Add:2
LINE SMC/Plant (Googol Tech):1 -> SMC/Derivative1:1
LINE SMC/Plant (Googol Tech):1 -> SMC/Gain1:1
LINE SMC/Plant (Googol Tech):1 -> SMC/Goto3:1
LINE SMC/Ref. Position, Xref (mm)1:1 -> SMC/Add5:1
LINE SMC/Ref. Position, Xref (mm)1:1 -> SMC/Goto5:1
LINE SMC/Ref. Position, Xref (mm)1:1 -> SMC/Subsystem1:1
LINE SMC/Ref. Position, Xref (mm):1 -> SMC/Add:1
LINE SMC/Ref. Position, Xref (mm):1 -> SMC/Goto1:1
LINE SMC/Ref. Position, Xref (mm):1 -> SMC/Subsystem:1
LINE SMC/Reference Input:1 -> SMC/Scope:3
LINE SMC/Saturation1:1 -> SMC/Plant (Googol Tech)1:1
LINE SMC/Saturation:1 -> SMC/Plant (Googol Tech):1
LINE SMC/Sign1:1 -> SMC/Gain (K)1:1
LINE SMC/Sign:1 -> SMC/Gain (K):1
LINE SMC/Subsystem/Derivative2:1 -> SMC/Subsystem/Derivative3:1
LINE SMC/Subsystem/Derivative2:1 -> SMC/Subsystem/y_dot:1
LINE SMC/Subsystem/Derivative3:1 -> SMC/Subsystem/y_ddot:1
LINE SMC/Subsystem/yd:1 -> SMC/Subsystem/Derivative2:1
LINE SMC/Subsystem1/Derivative1:1 -> SMC/Subsystem1/yd_3dot:1
LINE SMC/Subsystem1/Derivative2:1 -> SMC/Subsystem1/Derivative3:1
LINE SMC/Subsystem1/Derivative2:1 -> SMC/Subsystem1/yd_dot:1
LINE SMC/Subsystem1/Derivative3:1 -> SMC/Subsystem1/Derivative1:1
LINE SMC/Subsystem1/Derivative3:1 -> SMC/Subsystem1/yd_ddot:1
LINE SMC/Subsystem1/yd:1 -> SMC/Subsystem1/Derivative2:1
LINE SMC/Subsystem1:1 -> SMC/Add6:1
LINE SMC/Subsystem1:2 -> SMC/Add10:1
LINE SMC/Subsystem1:3 -> SMC/Gain2:1
LINE SMC/Subsystem2/Derivative1:1 -> SMC/Subsystem2/Derivative2:1
LINE SMC/Subsystem2/Derivative1:1 -> SMC/Subsystem2/y_ddot:1
LINE SMC/Subsystem2/Derivative2:1 -> SMC/Subsystem2/y_3dot:1
LINE SMC/Subsystem2/Derivative3:1 -> SMC/Subsystem2/Derivative1:1
LINE SMC/Subsystem2/Derivative3:1 -> SMC/Subsystem2/y_dot:1
LINE SMC/Subsystem2/y:1 -> SMC/Subsystem2/Derivative3:1
LINE SMC/Subsystem2:1 -> SMC/Add6:2
LINE SMC/Subsystem2:1 -> SMC/Lamda5:1
LINE SMC/Subsystem2:2 -> SMC/Add10:2
LINE SMC/Subsystem2:2 -> SMC/Lamda3:1
LINE SMC/Subsystem2:3 -> SMC/Terminator:1
LINE SMC/Subsystem:1 -> SMC/Add4:3
LINE SMC/Subsystem:2 -> SMC/Add1:2
LINE SMC/Sum1:1 -> SMC/Saturation1:1
LINE SMC/Sum2:1 -> SMC/Sign1:1
LINE SMC/Sum:1 -> SMC/Saturation:1
LINE SMC/TIme Delay1:1 -> SMC/Actual position1:1
LINE SMC/TIme Delay1:1 -> SMC/Add5:2
LINE SMC/TIme Delay1:1 -> SMC/Gain7:1
LINE SMC/TIme Delay1:1 -> SMC/Goto7:1
LINE SMC/TIme Delay1:1 -> SMC/Subsystem2:1
